# Revit family: xBathtub-Freestanding-DXV-Oak_Hill-D12025014.239
name_source: partatom
category: Plumbing Fixtures
revit_build: Autodesk Revit 2014 (Build: 20130308_1515(x64)
units: mm (PartAtom-declared; Revit-internal decimal feet)

## types (1)
- D12025014.239
    Assembly Code = D2010510
    CW Connection = Yes
    CWFU = 3
    Default Elevation = 0"
    Description = Oak Hill Freestanding Soaking Tub With Feet
    HW Connection = Yes
    HWFU = 3
    Height = 29 3/4"
    Installation Type = Freestanding
    Length = 66"
    Manufacturer = DXV
    Material = Acrylic-DXV-415-Canvas White
    Model = D12025014.239
    Price = Prices may vary. Please consult Manufacturer Representative for most up-to-date price list.
    Product Documentation Link = https://dxv01.blob.core.windows.net
    Product Page URL = https://www.dxv.com
    URL = http://www.dxv.com
    Vent Connection = No
    WFU = 4
    Warranty Documentation Link = https://www.dxv.com
    Waste Connection = Yes
    Waste Connection Diameter = 2 1/8"
    Waste Connection Radius = 1 1/16"
    Width = 36"

## geometry (parser evidence)
native form markers: Sweep x1
no freeform markers — native parametric forms only
